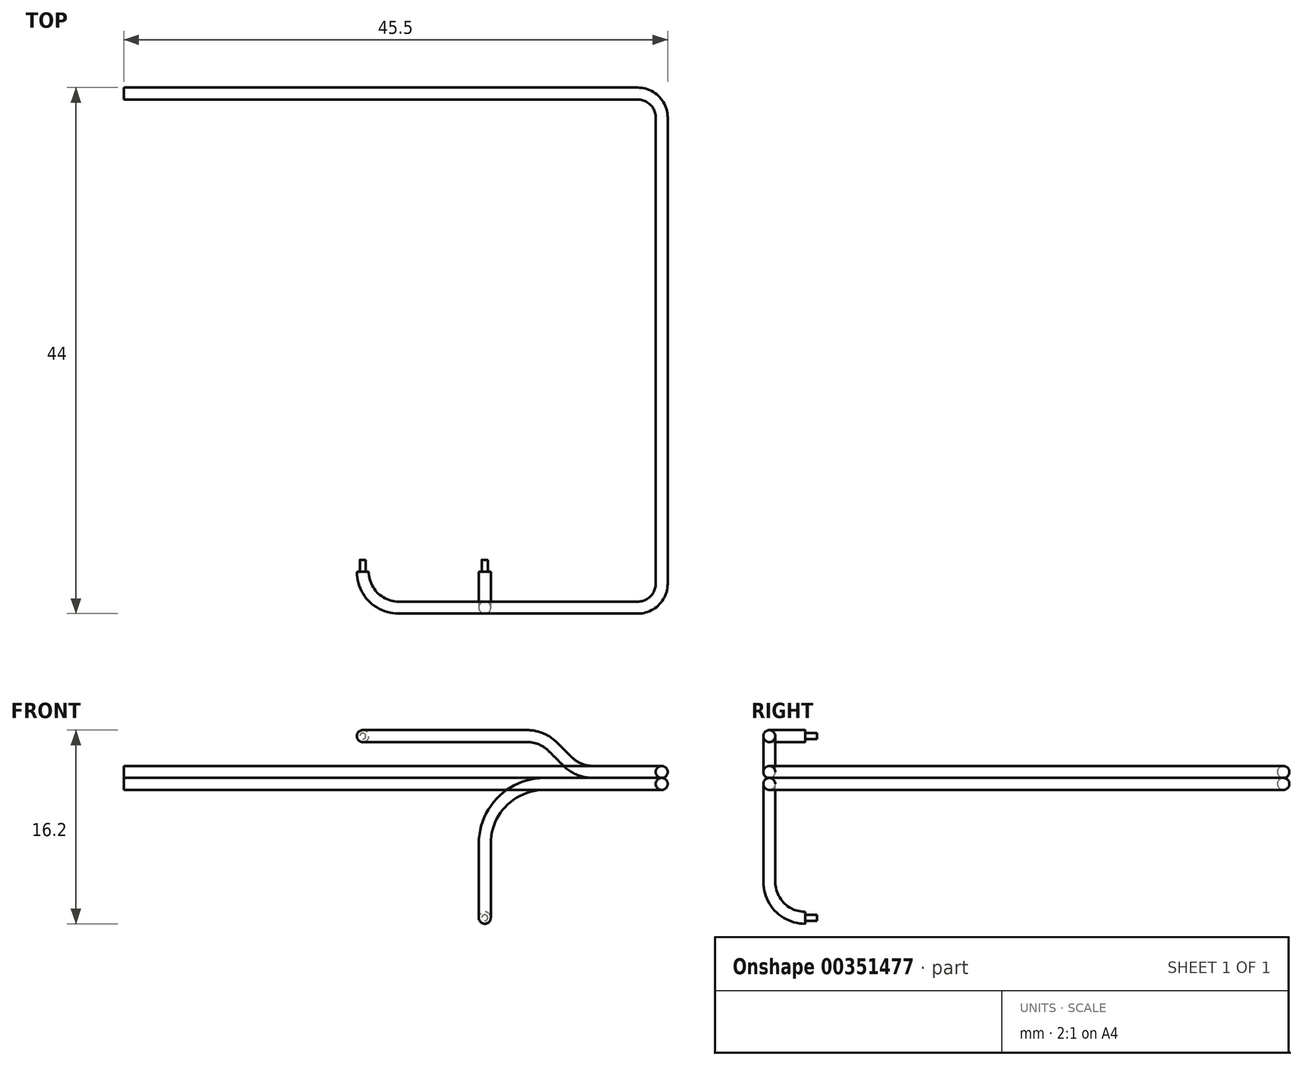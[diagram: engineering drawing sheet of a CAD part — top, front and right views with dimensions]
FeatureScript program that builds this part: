
annotation { "Feature Type Name" : "Feature", "Feature Type Description" : "" }
export const myFeature = defineFeature(function(context is Context, id is Id, definition is map)
    precondition{}
    {
        {
            var Q0;
            Q0=qCreatedBy(makeId("Top.planeOp"),FACE);
            var sketch = newSketch(context, id + "F0", { "sketchPlane" : qUnion([Q0])});
            skLineSegment(sketch, "E0", {"start": v(0, 0) * mm, "end": v(1, 0) * mm});
            skLineSegment(sketch, "E1", {"start": v(1, 0) * mm, "end": v(23, 0) * mm});
            skLineSegment(sketch, "E2", {"start": v(25, 2) * mm, "end": v(25, 41) * mm});
            skLineSegment(sketch, "E3", {"start": v(23, 43) * mm, "end": v(-20, 43) * mm});
            skPoint(sketch, "E4.visualSharp", {"position": v(25, 0) * mm});
            skArc(sketch, "E4.filletArc", {"start": v(23, 0) * mm, "mid": v(24.41, 0.59) * mm, "end": v(25, 2) * mm});
            skPoint(sketch, "E5.visualSharp", {"position": v(25, 43) * mm});
            skArc(sketch, "E5.filletArc", {"start": v(25, 41) * mm, "mid": v(24.41, 42.41) * mm, "end": v(23, 43) * mm});
            skSolve(sketch);
        }
        {
            var Q0;
            Q0=qCreatedBy(makeId("Right.planeOp"),FACE);
            var Q1;
            Q1=sQuery(id+"F0.wireOp",VERTEX,"E4.filletArc.start");
            cPlane(context, id + "F1", {"entities" : qUnion([Q0, Q1]), "cplaneType" : CPlaneType.PLANE_POINT, "offset" : 25 * mm, "width" : 150 * mm, "height" : 150 * mm});
        }
        {
            var Q0;
            Q0=qCreatedBy(id+"F1.planeOp",FACE);
            var sketch = newSketch(context, id + "F2", { "sketchPlane" : qUnion([Q0])});
            skCircle(sketch, "E6", {"center": v(0, 0) * mm, "radius": 0.5 * mm});
            skCircle(sketch, "E7", {"center": v(0, 1) * mm, "radius": 0.5 * mm});
            skSolve(sketch);
        }
        {
            var Q0;
            Q0 = qSketchRegion(id + "F2", true);
            var Q1;
            Q1=sQuery(id+"F0.wireOp",EDGE,"E4.filletArc");
            var Q2;
            Q2=sQuery(id+"F0.wireOp",EDGE,"E2");
            var Q3;
            Q3=sQuery(id+"F0.wireOp",EDGE,"E5.filletArc");
            var Q4;
            Q4=sQuery(id+"F0.wireOp",EDGE,"E3");
            sweep(context, id + "F3", {"profiles" : qUnion([Q0]), "path" : qUnion([Q1, Q2, Q3, Q4])});
        }
        {
            var Q0;
            Q0=qCreatedBy(makeId("Front.planeOp"),FACE);
            var sketch = newSketch(context, id + "F4", { "sketchPlane" : qUnion([Q0])});
            skPoint(sketch, "E8.0", {"position": v(23, 1) * mm});
            skLineSegment(sketch, "E9", {"start": v(23, 1) * mm, "end": v(19.24, 1) * mm});
            skLineSegment(sketch, "E10", {"start": v(17.12, 1.88) * mm, "end": v(15.88, 3.12) * mm});
            skLineSegment(sketch, "E11", {"start": v(13.76, 4) * mm, "end": v(3, 4) * mm});
            skPoint(sketch, "E12.visualSharp", {"position": v(18, 1) * mm});
            skArc(sketch, "E12.filletArc", {"start": v(17.12, 1.88) * mm, "mid": v(18.1, 1.23) * mm, "end": v(19.24, 1) * mm});
            skPoint(sketch, "E13.visualSharp", {"position": v(15, 4) * mm});
            skArc(sketch, "E13.filletArc", {"start": v(15.88, 3.12) * mm, "mid": v(14.9, 3.77) * mm, "end": v(13.76, 4) * mm});
            skSolve(sketch);
        }
        {
            var Q0;
            Q0=makeQuery(id+"F2.imprint","IMPRINT",FACE,{"disambiguationData":[TD([[makeQuery(id+"F2.imprint","IMPRINT",EDGE,{"derivedFrom":sQuery(id+"F2.wireOp",EDGE,"E7")}),1.0]])]});
            var Q1;
            Q1 = qConstructionFilter(qBodyType(qCreatedBy(id + "F4" ,EDGE), BodyType.WIRE), ConstructionObject.NO);
            sweep(context, id + "F5", {"operationType" : NewBodyOperationType.ADD, "profiles" : qUnion([Q0]), "path" : qUnion([Q1])});
        }
        {
            var Q0;
            Q0=qCreatedBy(makeId("Top.planeOp"),FACE);
            var Q1;
            Q1=sQuery(id+"F4.wireOp",VERTEX,"E11.end");
            cPlane(context, id + "F6", {"entities" : qUnion([Q0, Q1]), "cplaneType" : CPlaneType.PLANE_POINT, "offset" : 25 * mm, "width" : 150 * mm, "height" : 150 * mm});
        }
        {
            var Q0;
            Q0=qCreatedBy(id+"F6.planeOp",FACE);
            var sketch = newSketch(context, id + "F7", { "sketchPlane" : qUnion([Q0])});
            skPoint(sketch, "E14.0", {"position": v(23, 0) * mm});
            skLineSegment(sketch, "E15", {"start": v(23, 0) * mm, "end": v(3, 0) * mm});
            skLineSegment(sketch, "E16", {"start": v(0, 3) * mm, "end": v(0, 4) * mm});
            skPoint(sketch, "E17.visualSharp", {"position": v(0, 0) * mm});
            skArc(sketch, "E17.filletArc", {"start": v(0, 3) * mm, "mid": v(0.88, 0.88) * mm, "end": v(3, 0) * mm});
            skSolve(sketch);
        }
        {
            var Q0;
            Q0=makeQuery(id+"F5.opSweep","CAP_FACE",FACE,{"disambiguationData":[OSD([sQuery(id+"F2.wireOp",EDGE,"E7"),sQuery(id+"F4.wireOp",VERTEX,"E11.end")])],"isStart":false});
            var Q1;
            Q1=sQuery(id+"F7.wireOp",EDGE,"E17.filletArc");
            sweep(context, id + "F8", {"operationType" : NewBodyOperationType.ADD, "profiles" : qUnion([Q0]), "path" : qUnion([Q1])});
        }
        {
            var Q0;
            Q0=qCreatedBy(makeId("Front.planeOp"),FACE);
            var sketch = newSketch(context, id + "F9", { "sketchPlane" : qUnion([Q0])});
            skPoint(sketch, "E18.0", {"position": v(23, 0) * mm});
            skLineSegment(sketch, "E19", {"start": v(23, 0) * mm, "end": v(15.2, 0) * mm});
            skLineSegment(sketch, "E20", {"start": v(10.2, -5) * mm, "end": v(10.2, -8.2) * mm});
            skPoint(sketch, "E21.visualSharp", {"position": v(10.2, 0) * mm});
            skArc(sketch, "E21.filletArc", {"start": v(15.2, 0) * mm, "mid": v(11.66, -1.46) * mm, "end": v(10.2, -5) * mm});
            skSolve(sketch);
        }
        {
            var Q0;
            Q0=makeQuery(id+"F2.imprint","IMPRINT",FACE,{"disambiguationData":[TD([[makeQuery(id+"F2.imprint","IMPRINT",EDGE,{"derivedFrom":sQuery(id+"F2.wireOp",EDGE,"E6")}),1.0]])]});
            var Q1;
            Q1=sQuery(id+"F9.wireOp",EDGE,"E19");
            var Q2;
            Q2=sQuery(id+"F9.wireOp",EDGE,"E21.filletArc");
            var Q3;
            Q3=sQuery(id+"F9.wireOp",EDGE,"E20");
            sweep(context, id + "F10", {"operationType" : NewBodyOperationType.ADD, "profiles" : qUnion([Q0]), "path" : qUnion([Q1, Q2, Q3])});
        }
        {
            var Q0;
            Q0=qCreatedBy(makeId("Right.planeOp"),FACE);
            var Q1;
            Q1=sQuery(id+"F9.wireOp",VERTEX,"E20.end");
            cPlane(context, id + "F11", {"entities" : qUnion([Q0, Q1]), "cplaneType" : CPlaneType.PLANE_POINT, "offset" : 25 * mm, "width" : 150 * mm, "height" : 150 * mm});
        }
        {
            var Q0;
            Q0=qCreatedBy(id+"F11.planeOp",FACE);
            var sketch = newSketch(context, id + "F12", { "sketchPlane" : qUnion([Q0])});
            skPoint(sketch, "E22.0", {"position": v(0, -8.2) * mm});
            skArc(sketch, "E23", {"start": v(0, -8.2) * mm, "mid": v(0.88, -10.32) * mm, "end": v(3, -11.2) * mm});
            skLineSegment(sketch, "E24", {"start": v(0, -8.2) * mm, "end": v(0, -4.31) * mm, "construction": true});
            skLineSegment(sketch, "E25", {"start": v(3, -11.2) * mm, "end": v(4, -11.2) * mm});
            skSolve(sketch);
        }
        {
            var Q0;
            Q0=makeQuery(id+"F10.opSweep","CAP_FACE",FACE,{"disambiguationData":[OSD([sQuery(id+"F2.wireOp",EDGE,"E6"),sQuery(id+"F9.wireOp",VERTEX,"E20.end")])],"isStart":false});
            var Q1;
            Q1=sQuery(id+"F12.wireOp",EDGE,"E23");
            sweep(context, id + "F13", {"operationType" : NewBodyOperationType.ADD, "profiles" : qUnion([Q0]), "path" : qUnion([Q1])});
        }
        {
            var Q0;
            Q0=makeQuery(id+"F13.opSweep","CAP_FACE",FACE,{"disambiguationData":[OSD([sQuery(id+"F2.wireOp",EDGE,"E6"),sQuery(id+"F9.wireOp",VERTEX,"E20.end"),sQuery(id+"F12.wireOp",VERTEX,"E23.end")])],"isStart":false});
            var sketch = newSketch(context, id + "F14", { "sketchPlane" : qUnion([Q0])});
            skPoint(sketch, "E26.0", {"position": v(0, 4) * mm});
            skPoint(sketch, "E27.0", {"position": v(-10.2, -11.2) * mm});
            skCircle(sketch, "E28", {"center": v(0, 4) * mm, "radius": 0.25 * mm});
            skCircle(sketch, "E29", {"center": v(-10.2, -11.2) * mm, "radius": 0.25 * mm});
            skSolve(sketch);
        }
        {
            var Q0;
            Q0 = qSketchRegion(id + "F14", true);
            var Q1;
            Q1=sQuery(id+"F7.wireOp",EDGE,"E16");
            sweep(context, id + "F15", {"operationType" : NewBodyOperationType.ADD, "profiles" : qUnion([Q0]), "path" : qUnion([Q1])});
        }
    });
